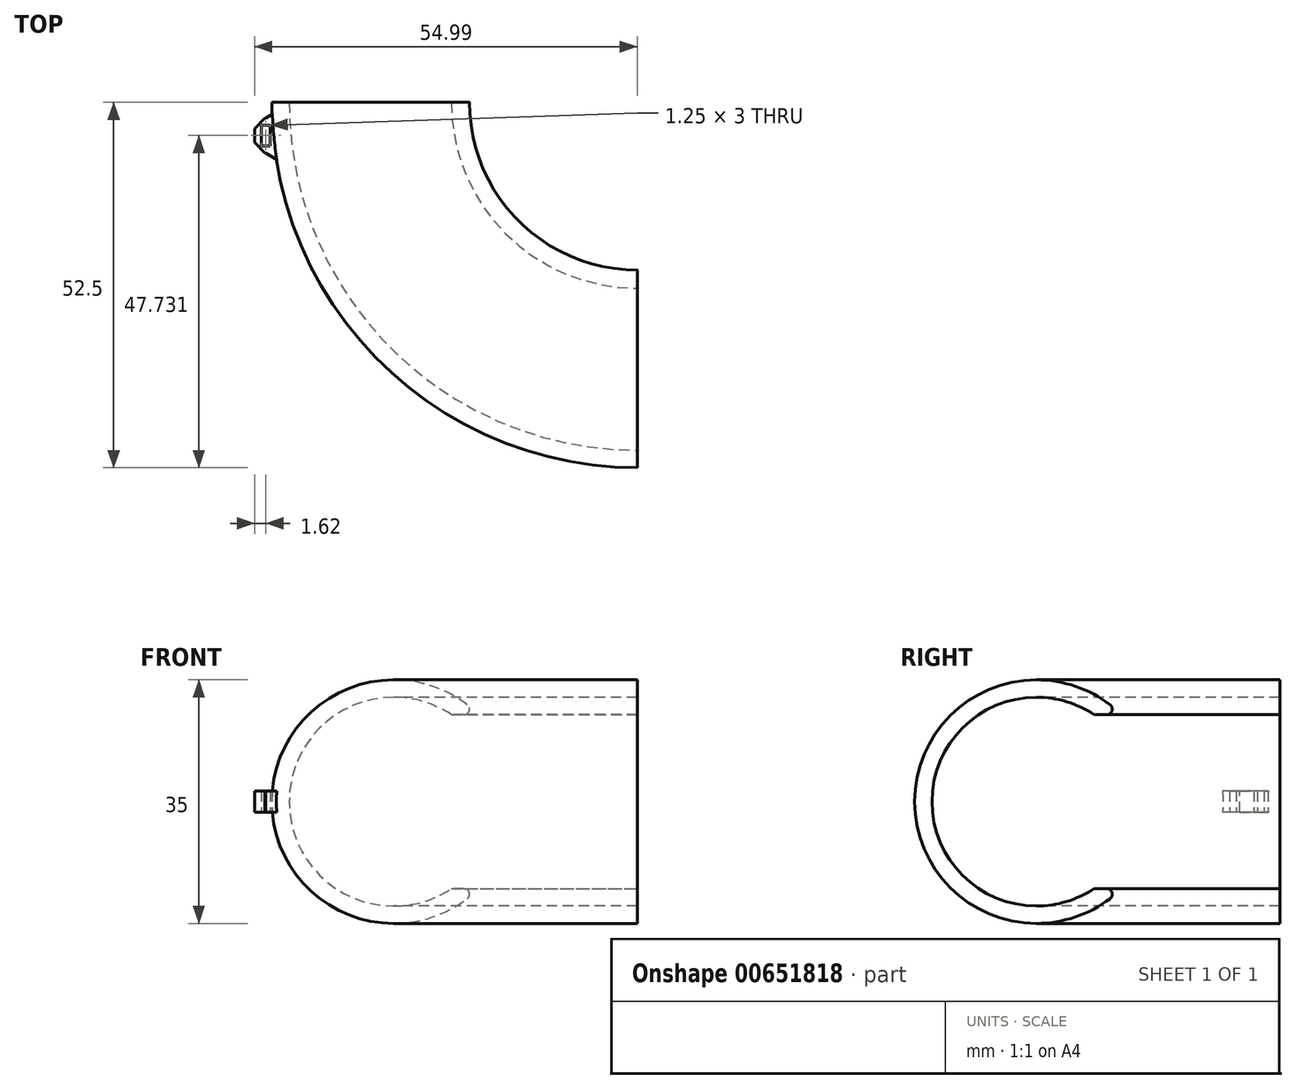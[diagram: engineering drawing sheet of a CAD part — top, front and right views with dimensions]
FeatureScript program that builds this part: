
annotation { "Feature Type Name" : "Feature", "Feature Type Description" : "" }
export const myFeature = defineFeature(function(context is Context, id is Id, definition is map)
    precondition{}
    {
        {
            var Q0;
            Q0=qCreatedBy(makeId("Front.planeOp"),FACE);
            var sketch = newSketch(context, id + "F0", { "sketchPlane" : qUnion([Q0])});
            skCircle(sketch, "E0", {"center": v(-35, 0) * mm, "radius": 15 * mm});
            skCircle(sketch, "E1", {"center": v(-35, 0) * mm, "radius": 17.5 * mm});
            skLineSegment(sketch, "E2.bottom", {"start": v(-2.5, -12.5) * mm, "end": v(-32.5, -12.5) * mm});
            skLineSegment(sketch, "E2.top", {"start": v(-2.5, 12.5) * mm, "end": v(-32.5, 12.5) * mm});
            skLineSegment(sketch, "E2.left", {"start": v(-2.5, -12.5) * mm, "end": v(-2.5, 12.5) * mm});
            skLineSegment(sketch, "E2.right", {"start": v(-32.5, -12.5) * mm, "end": v(-32.5, 12.5) * mm});
            skPoint(sketch, "E2.middle", {"position": v(-17.5, 0) * mm});
            skLineSegment(sketch, "E3", {"start": v(-26.7, 12.5) * mm, "end": v(-24.91, 14.3) * mm});
            skLineSegment(sketch, "E4", {"start": v(-26.7, -12.5) * mm, "end": v(-24.91, -14.3) * mm});
            skSolve(sketch);
        }
        {
            var Q0;
            Q0=qCreatedBy(makeId("Right.planeOp"),FACE);
            var sketch = newSketch(context, id + "F1", { "sketchPlane" : qUnion([Q0])});
            skCircle(sketch, "E5", {"center": v(-35, 0) * mm, "radius": 15 * mm});
            skCircle(sketch, "E6", {"center": v(-35, 0) * mm, "radius": 17.5 * mm});
            skLineSegment(sketch, "E7.bottom", {"start": v(-2.5, -12.5) * mm, "end": v(-32.5, -12.5) * mm});
            skLineSegment(sketch, "E7.top", {"start": v(-2.5, 12.5) * mm, "end": v(-32.5, 12.5) * mm});
            skLineSegment(sketch, "E7.left", {"start": v(-2.5, -12.5) * mm, "end": v(-2.5, 12.5) * mm});
            skLineSegment(sketch, "E7.right", {"start": v(-32.5, -12.5) * mm, "end": v(-32.5, 12.5) * mm});
            skPoint(sketch, "E7.middle", {"position": v(-17.5, 0) * mm});
            skLineSegment(sketch, "E8", {"start": v(-26.7, 12.5) * mm, "end": v(-24.91, 14.3) * mm});
            skLineSegment(sketch, "E9", {"start": v(-26.7, -12.5) * mm, "end": v(-24.91, -14.3) * mm});
            skSolve(sketch);
        }
        {
            var Q0;
            Q0=qCreatedBy(makeId("Top.planeOp"),FACE);
            var sketch = newSketch(context, id + "F2", { "sketchPlane" : qUnion([Q0])});
            skArc(sketch, "E10", {"start": v(-35, 0) * mm, "mid": v(-24.75, -24.75) * mm, "end": v(0, -35) * mm});
            skSolve(sketch);
        }
        {
            var Q0;
            {var subQ0=sQuery(id+"F1.wireOp",EDGE,"E7.bottom");var subQ1=sQuery(id+"F1.wireOp",EDGE,"E5");var subQ2=makeQuery(id+"F1.imprint","INTERSECT",VERTEX,{"derivedFrom":[subQ1,subQ0]});Q0=makeQuery(id+"F1.imprint","IMPRINT",FACE,{"disambiguationData":[TD([[makeQuery(id+"F1.imprint","IMPRINT",EDGE,{"disambiguationData":[TD([[subQ2,1.0]])],"derivedFrom":subQ1}),-1.0]])]});}
            var Q1;
            {var subQ0=sQuery(id+"F0.wireOp",EDGE,"E2.bottom");var subQ1=sQuery(id+"F0.wireOp",EDGE,"E0");var subQ2=makeQuery(id+"F0.imprint","INTERSECT",VERTEX,{"derivedFrom":[subQ1,subQ0]});Q1=makeQuery(id+"F0.imprint","IMPRINT",FACE,{"disambiguationData":[TD([[makeQuery(id+"F0.imprint","IMPRINT",EDGE,{"disambiguationData":[TD([[subQ2,1.0]])],"derivedFrom":subQ1}),-1.0]])]});}
            var Q2;
            {var subQ0=sQuery(id+"F0.wireOp",EDGE,"E3");Q2=makeQuery(id+"F0.imprint","IMPRINT",FACE,{"disambiguationData":[TD([[makeQuery(id+"F0.imprint","IMPRINT",EDGE,{"derivedFrom":subQ0}),-1.0]])]});}
            var Q3;
            {var subQ0=sQuery(id+"F0.wireOp",EDGE,"E4");Q3=makeQuery(id+"F0.imprint","IMPRINT",FACE,{"disambiguationData":[TD([[makeQuery(id+"F0.imprint","IMPRINT",EDGE,{"derivedFrom":subQ0}),1.0]])]});}
            var Q4;
            {var subQ0=sQuery(id+"F1.wireOp",EDGE,"E8");Q4=makeQuery(id+"F1.imprint","IMPRINT",FACE,{"disambiguationData":[TD([[makeQuery(id+"F1.imprint","IMPRINT",EDGE,{"derivedFrom":subQ0}),-1.0]])]});}
            var Q5;
            {var subQ0=sQuery(id+"F1.wireOp",EDGE,"E9");Q5=makeQuery(id+"F1.imprint","IMPRINT",FACE,{"disambiguationData":[TD([[makeQuery(id+"F1.imprint","IMPRINT",EDGE,{"derivedFrom":subQ0}),1.0]])]});}
            var Q6;
            Q6=sQuery(id+"F2.wireOp",EDGE,"E10");
            sweep(context, id + "F3", {"profiles" : qUnion([Q0, Q1, Q2, Q3, Q4, Q5]), "path" : qUnion([Q6])});
        }
        {
            var Q0;
            Q0=makeQuery(id+"F3.opSweep","SWEPT_BODY",BODY,{"disambiguationData":[OSD([sQuery(id+"F1.wireOp",EDGE,"E5"),sQuery(id+"F1.wireOp",EDGE,"E6"),sQuery(id+"F1.wireOp",EDGE,"E8"),sQuery(id+"F1.wireOp",EDGE,"E9"),sQuery(id+"F2.wireOp",EDGE,"E10")])]});
            deleteBodies(context, id + "F4", {"entities" : qUnion([Q0])});
        }
        {
            var Q0;
            Q0=makeQuery(id+"F3.opSweep","SWEPT_EDGE",EDGE,{"disambiguationData":[OSD([sQuery(id+"F0.wireOp",EDGE,"E1"),sQuery(id+"F0.wireOp",EDGE,"E2.bottom"),sQuery(id+"F2.wireOp",EDGE,"E10")])]});
            var Q1;
            Q1=makeQuery(id+"F3.opSweep","SWEPT_EDGE",EDGE,{"disambiguationData":[OSD([sQuery(id+"F0.wireOp",EDGE,"E1"),sQuery(id+"F0.wireOp",EDGE,"E2.top"),sQuery(id+"F2.wireOp",EDGE,"E10")])]});
            fillet(context, id + "F5", {"entities" : qUnion([Q0, Q1]), "radius" : .8 * mm, "tangentPropagation" : true, "allowEdgeOverflow" : false});
        }
        {
            var Q0;
            Q0=qCreatedBy(makeId("Top.planeOp"),FACE);
            var sketch = newSketch(context, id + "F6", { "sketchPlane" : qUnion([Q0])});
            skLineSegment(sketch, "E11.bottom", {"start": v(-52.74, -2.27) * mm, "end": v(-51.74, -2.27) * mm});
            skLineSegment(sketch, "E11.top", {"start": v(-52.74, -7.27) * mm, "end": v(-51.74, -7.27) * mm});
            skLineSegment(sketch, "E11.left", {"start": v(-52.74, -2.27) * mm, "end": v(-52.74, -7.27) * mm});
            skLineSegment(sketch, "E11.right", {"start": v(-51.74, -2.27) * mm, "end": v(-51.74, -7.27) * mm});
            skPoint(sketch, "E11.middle", {"position": v(-52.24, -4.77) * mm});
            skLineSegment(sketch, "E12.bottom", {"start": v(-54, -7.27) * mm, "end": v(-55, -7.27) * mm});
            skLineSegment(sketch, "E12.top", {"start": v(-54, -2.27) * mm, "end": v(-55, -2.27) * mm});
            skLineSegment(sketch, "E12.left", {"start": v(-54, -7.27) * mm, "end": v(-54, -2.27) * mm});
            skLineSegment(sketch, "E12.right", {"start": v(-55, -7.27) * mm, "end": v(-55, -2.27) * mm});
            skLineSegment(sketch, "E13", {"start": v(-52.74, -7.27) * mm, "end": v(-54, -7.27) * mm});
            skLineSegment(sketch, "E14", {"start": v(-54, -6.27) * mm, "end": v(-52.74, -6.27) * mm});
            skLineSegment(sketch, "E15", {"start": v(-52.74, -6.27) * mm, "end": v(-52.74, -2.27) * mm});
            skLineSegment(sketch, "E16", {"start": v(-54, -2.27) * mm, "end": v(-54, -3.27) * mm});
            skLineSegment(sketch, "E17", {"start": v(-54, -3.27) * mm, "end": v(-52.74, -3.27) * mm});
            skLineSegment(sketch, "E18", {"start": v(-52.74, -2.27) * mm, "end": v(-54, -2.27) * mm});
            skLineSegment(sketch, "E19", {"start": v(-55, -6.27) * mm, "end": v(-51.74, -8.27) * mm});
            skLineSegment(sketch, "E20", {"start": v(-51.74, -8.27) * mm, "end": v(-51.74, -7.27) * mm});
            skLineSegment(sketch, "E21", {"start": v(-55, -3.27) * mm, "end": v(-51.74, -1.27) * mm});
            skLineSegment(sketch, "E22", {"start": v(-51.74, -1.27) * mm, "end": v(-51.74, -2.27) * mm});
            skSolve(sketch);
        }
        {
            var Q0;
            Q0 = qSketchRegion(id + "F6", true);
            extrude(context, id + "F7", {"entities" : qUnion([Q0]), "operationType" : NewBodyOperationType.ADD, "endBound" : BoundingType.SYMMETRIC, "depth" : 3 * mm, "offsetDistance" : 25 * mm});
        }
        {
            var Q0;
            Q0=qCreatedBy(makeId("Right.planeOp"),FACE);
            var Q1;
            Q1=qCreatedBy(makeId("Front.planeOp"),FACE);
            cPlane(context, id + "F8", {"entities" : qUnion([Q0, Q1]), "cplaneType" : CPlaneType.MID_PLANE, "offset" : 25 * mm, "flipAlignment" : true, "width" : 150 * mm, "height" : 150 * mm});
        }
        {
            var Q0;
            Q0=makeQuery(id+"FEbmQs7poKJpS70_1.1.F7.opExtrude","SWEPT_EDGE",EDGE,{"disambiguationData":[OSD([sQuery(id+"F6.wireOp",EDGE,"E12.top"),sQuery(id+"F6.wireOp",EDGE,"E12.right")])]});
            var Q1;
            Q1=makeQuery(id+"FEbmQs7poKJpS70_1.1.F7.opExtrude","SWEPT_EDGE",EDGE,{"disambiguationData":[OSD([sQuery(id+"F6.wireOp",EDGE,"E12.bottom"),sQuery(id+"F6.wireOp",EDGE,"E12.right")])]});
            var Q2;
            Q2=makeQuery(id+"F7.opExtrude","SWEPT_EDGE",EDGE,{"disambiguationData":[OSD([sQuery(id+"F6.wireOp",EDGE,"E12.bottom"),sQuery(id+"F6.wireOp",EDGE,"E12.right")])]});
            var Q3;
            Q3=makeQuery(id+"F7.opExtrude","SWEPT_EDGE",EDGE,{"disambiguationData":[OSD([sQuery(id+"F6.wireOp",EDGE,"E12.top"),sQuery(id+"F6.wireOp",EDGE,"E12.right")])]});
            chamfer(context, id + "F9", {"entities" : qUnion([Q0, Q1, Q2, Q3]), "width" : 1.5 * mm, "tangentPropagation" : true});
        }
    });
